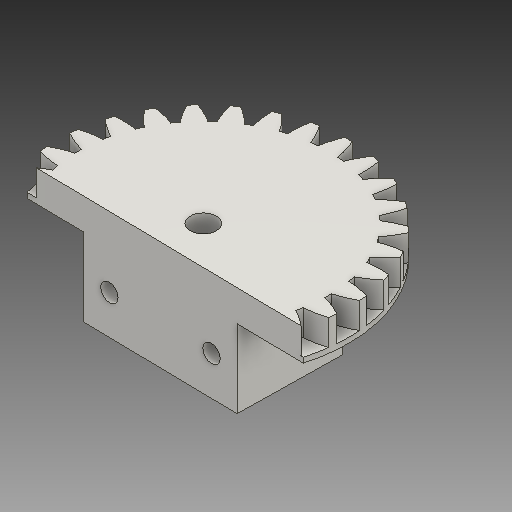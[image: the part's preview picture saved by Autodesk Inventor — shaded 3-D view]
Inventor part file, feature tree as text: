
AUTODESK INVENTOR PART (.ipt)
format: ipt  version: 2018 (Build 220112000, 112)  size: 292,864 bytes
history: native  units: mm
features: other x13, sketch x9, plane x4
ambient origin geometry x8: Origin, YZ Plane, XZ Plane, XY Plane, X Axis, Y Axis, Z Axis, Center Point
bodies: Volumenkörper1 (feature_tree)
feature tree (26):
  other  "Stirnzahnrad1"
  other  "Solid1::Stirnzahnrad1"
  other  "Bezeichnung1"
  sketch  "Sketch1"  dims[d0=10.0mm]
  sketch  "Sketch2"  dims[d16=40.0mm d17=0.0mm d41=0.0mm d43=40.0mm d46=40.0mm d47=0.0mm d48=0.0mm]
  sketch  "Skizze9"
  sketch  "Skizze10"
  sketch  "Skizze11"
  sketch  "Skizze12"
  sketch  "Skizze13"
  sketch  "Skizze14"
  sketch  "Skizze15"
  plane  "XZ Plane_1"
  plane  "Work Plane2"
  plane  "Work Plane8"
  plane  "Work Plane9"
  other  "Z Axis_1"
  other  "Flä1"
  other  "Srf1::Abgeleitet"
  other  "Abstands-iMate"
  other  "Ausrichtungs-iMate"
  other  "Netz-iMate"
  other  "Achsen-iMate"
  other  "Positions-iMate"
  other  "Netz-iMate 2"
  other  "Startebenen-iMate"
